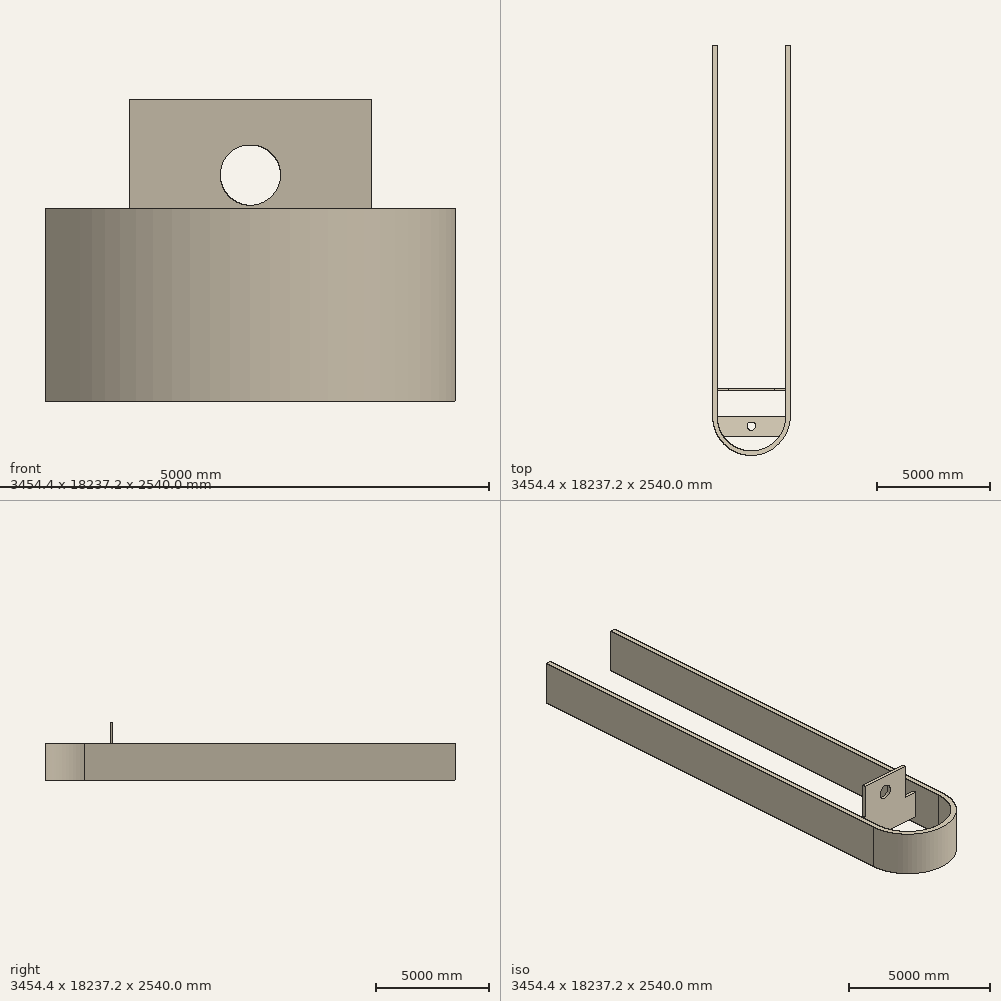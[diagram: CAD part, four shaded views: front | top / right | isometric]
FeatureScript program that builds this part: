
annotation { "Feature Type Name" : "Feature", "Feature Type Description" : "" }
export const myFeature = defineFeature(function(context is Context, id is Id, definition is map)
    precondition{}
    {
        {
            var Q0;
            Q0=qCreatedBy(makeId("Top.planeOp"),FACE);
            var sketch = newSketch(context, id + "F0", { "sketchPlane" : qUnion([Q0])});
            skLineSegment(sketch, "E0", {"start": v(-1727.2, 0) * mm, "end": v(-1524, 0) * mm});
            skLineSegment(sketch, "E1", {"start": v(-1524, 0) * mm, "end": v(-1524, -1270) * mm});
            skLineSegment(sketch, "E2", {"start": v(-1727.2, 0) * mm, "end": v(-1727.2, -1270) * mm});
            skPoint(sketch, "E3.end.orphan", {"position": v(0, -2403.06) * mm});
            skLineSegment(sketch, "E4", {"start": v(1524, -1270) * mm, "end": v(1524, 0) * mm});
            skLineSegment(sketch, "E5", {"start": v(1524, 0) * mm, "end": v(1727.2, 0) * mm});
            skArc(sketch, "E6", {"start": v(1524, -1270) * mm, "mid": v(0, -2794) * mm, "end": v(-1524, -1270) * mm});
            skArc(sketch, "E7", {"start": v(-1727.2, -1270) * mm, "mid": v(0, -2997.2) * mm, "end": v(1727.2, -1270) * mm});
            skLineSegment(sketch, "E8", {"start": v(1727.2, -1270) * mm, "end": v(1727.2, 0) * mm});
            skSolve(sketch);
        }
        {
            var Q0;
            Q0=makeQuery(id+"F0.imprint","IMPRINT",FACE,{"disambiguationData":[TD([[makeQuery(id+"F0.imprint","IMPRINT",EDGE,{"derivedFrom":sQuery(id+"F0.wireOp",EDGE,"E0")}),-1.0]])]});
            extrude(context, id + "F1", {"entities" : qUnion([Q0]), "depth" : 1625.6 * mm});
        }
        {
            var Q0;
            Q0=qCreatedBy(makeId("Front.planeOp"),FACE);
            var sketch = newSketch(context, id + "F2", { "sketchPlane" : qUnion([Q0])});
            skLineSegment(sketch, "E9", {"start": v(-1524, 1270) * mm, "end": v(-1016, 1270) * mm});
            skLineSegment(sketch, "E10", {"start": v(-1016, 1270) * mm, "end": v(-1016, 2540) * mm});
            skLineSegment(sketch, "E11", {"start": v(-1016, 2540) * mm, "end": v(0, 2540) * mm});
            skLineSegment(sketch, "E12", {"start": v(1524, 1270) * mm, "end": v(1016, 1270) * mm});
            skLineSegment(sketch, "E13", {"start": v(1016, 1270) * mm, "end": v(1016, 2540) * mm});
            skLineSegment(sketch, "E14", {"start": v(1016, 2540) * mm, "end": v(0, 2540) * mm});
            skLineSegment(sketch, "E15", {"start": v(-1524, 1270) * mm, "end": v(-1524, 254) * mm});
            skLineSegment(sketch, "E16", {"start": v(1524, 1270) * mm, "end": v(1524, 254) * mm});
            skLineSegment(sketch, "E17", {"start": v(-1524, 254) * mm, "end": v(1524, 254) * mm});
            skSolve(sketch);
        }
        {
            var Q0;
            Q0=makeQuery(id+"F2.imprint","IMPRINT",FACE,{"disambiguationData":[TD([[makeQuery(id+"F2.imprint","IMPRINT",EDGE,{"derivedFrom":sQuery(id+"F2.wireOp",EDGE,"ZSPI5Kq5-j5FG-L9A3-QIDn-ohDjtnUvU4sG")}),-1.0]])]});
            var Q1;
            Q1=makeQuery(id+"F2.imprint","IMPRINT",FACE,{"disambiguationData":[TD([[makeQuery(id+"F2.imprint","IMPRINT",EDGE,{"derivedFrom":sQuery(id+"F2.wireOp",EDGE,"E9")}),-1.0]])]});
            extrude(context, id + "F3", {"entities" : qUnion([Q0, Q1]), "operationType" : NewBodyOperationType.ADD, "depth" : 127 * mm});
        }
        {
            var Q0;
            Q0=makeQuery(id+"F3.boolean.opBoolean","MERGE",FACE,{"derivedFrom":[makeQuery(id+"F1.opExtrude","SWEPT_FACE",FACE,{"disambiguationData":[OSD([sQuery(id+"F0.wireOp",EDGE,"E0")])]}),makeQuery(id+"F1.opExtrude","SWEPT_FACE",FACE,{"disambiguationData":[OSD([sQuery(id+"F0.wireOp",EDGE,"E5")])]}),makeQuery(id+"F3.opExtrude","CAP_FACE",FACE,{"disambiguationData":[OSD([sQuery(id+"F2.wireOp",EDGE,"E9"),sQuery(id+"F2.wireOp",EDGE,"E10"),sQuery(id+"F2.wireOp",EDGE,"E11"),sQuery(id+"F2.wireOp",EDGE,"E12"),sQuery(id+"F2.wireOp",EDGE,"E13"),sQuery(id+"F2.wireOp",EDGE,"E14"),sQuery(id+"F2.wireOp",EDGE,"E15"),sQuery(id+"F2.wireOp",EDGE,"E16"),sQuery(id+"F2.wireOp",EDGE,"E17")])],"isStart":true})]});
            var sketch = newSketch(context, id + "F4", { "sketchPlane" : qUnion([Q0])});
            skPoint(sketch, "E18", {"position": v(0, 1905) * mm});
            skSolve(sketch);
        }
        {
            var Q0;
            Q0=sQuery(id+"F4.wireOp",VERTEX,"E18");
            var Q1;
            Q1=makeQuery(id+"F1.opExtrude","SWEPT_BODY",BODY,{"disambiguationData":[OSD([sQuery(id+"F0.wireOp",EDGE,"E0"),sQuery(id+"F0.wireOp",EDGE,"E1"),sQuery(id+"F0.wireOp",EDGE,"E2"),sQuery(id+"F0.wireOp",EDGE,"9GpaX0HQ-ANni-udGZ-ch0X-FV7p1uEIL64O"),sQuery(id+"F0.wireOp",EDGE,"6B0ilIzi-gSCg-tgtf-X7SF-Btb2jImptZIT"),sQuery(id+"F0.wireOp",EDGE,"E4"),sQuery(id+"F0.wireOp",EDGE,"BRMD6dyG-T5lG-EnZK-6NoF-wr3sixz7AlLv"),sQuery(id+"F0.wireOp",EDGE,"E5")])]});
            hole(context, id + "F5", {"style" : HoleStyle.SIMPLE, "endStyle" : HoleEndStyle.BLIND, "holeDiameter" : 508 * mm, "holeDepth" : 127 * mm, "isTappedThrough" : true, "tappedDepth" : 12.7 * mm, "tapClearance" : 3, "locations" : qUnion([Q0]), "scope" : qUnion([Q1])});
        }
        {
            var Q0;
            Q0=makeQuery(id+"F3.boolean.opBoolean","MERGE",FACE,{"derivedFrom":[makeQuery(id+"F1.opExtrude","SWEPT_FACE",FACE,{"disambiguationData":[OSD([sQuery(id+"F0.wireOp",EDGE,"E0")])]}),makeQuery(id+"F1.opExtrude","SWEPT_FACE",FACE,{"disambiguationData":[OSD([sQuery(id+"F0.wireOp",EDGE,"E5")])]}),makeQuery(id+"F3.opExtrude","CAP_FACE",FACE,{"disambiguationData":[OSD([sQuery(id+"F2.wireOp",EDGE,"E9"),sQuery(id+"F2.wireOp",EDGE,"E10"),sQuery(id+"F2.wireOp",EDGE,"E11"),sQuery(id+"F2.wireOp",EDGE,"E12"),sQuery(id+"F2.wireOp",EDGE,"E13"),sQuery(id+"F2.wireOp",EDGE,"E14"),sQuery(id+"F2.wireOp",EDGE,"E15"),sQuery(id+"F2.wireOp",EDGE,"E16"),sQuery(id+"F2.wireOp",EDGE,"E17")])],"isStart":true})]});
            var sketch = newSketch(context, id + "F6", { "sketchPlane" : qUnion([Q0])});
            skLineSegment(sketch, "E19.bottom", {"start": v(-1524, 1625.6) * mm, "end": v(-1524, 1625.6) * mm});
            skLineSegment(sketch, "E19.top", {"start": v(-1524, 0) * mm, "end": v(-1524, 0) * mm});
            skLineSegment(sketch, "E19.left", {"start": v(-1524, 1625.6) * mm, "end": v(-1524, 0) * mm});
            skLineSegment(sketch, "E19.right", {"start": v(-1524, 1625.6) * mm, "end": v(-1524, 0) * mm});
            skLineSegment(sketch, "E20.bottom", {"start": v(1524, 1625.6) * mm, "end": v(1727.2, 1625.6) * mm});
            skLineSegment(sketch, "E20.top", {"start": v(1524, 0) * mm, "end": v(1727.2, 0) * mm});
            skLineSegment(sketch, "E20.left", {"start": v(1524, 1625.6) * mm, "end": v(1524, 0) * mm});
            skLineSegment(sketch, "E20.right", {"start": v(1727.2, 1625.6) * mm, "end": v(1727.2, 0) * mm});
            skSolve(sketch);
        }
        {
            var Q0;
            {var subQ0=sQuery(id+"F0.wireOp",EDGE,"E5");var subQ2=makeQuery(id+"F1.opExtrude","CAP_EDGE",EDGE,{"disambiguationData":[OSD([subQ0])],"isStart":true});Q0=makeQuery(id+"F6.imprint","IMPRINT",FACE,{"disambiguationData":[TD([[makeQuery(id+"F6.imprint","IMPRINT",EDGE,{"derivedFrom":subQ2}),-1.0]])]});}
            var Q1;
            {var subQ1=sQuery(id+"F6.wireOp",EDGE,"E20.bottom");Q1=makeQuery(id+"F6.imprint","IMPRINT",FACE,{"disambiguationData":[TD([[makeQuery(id+"F6.imprint","IMPRINT",EDGE,{"derivedFrom":subQ1}),1.0]])]});}
            extrude(context, id + "F7", {"entities" : qUnion([Q0, Q1]), "operationType" : NewBodyOperationType.ADD, "depth" : 15240 * mm});
        }
        {
            var Q0;
            {var subQ0=sQuery(id+"F0.wireOp",EDGE,"E5");Q0=makeQuery(id+"F7.boolean.opBoolean","MERGE",FACE,{"derivedFrom":[makeQuery(id+"F1.opExtrude","CAP_FACE",FACE,{"disambiguationData":[OSD([sQuery(id+"F0.wireOp",EDGE,"E0"),sQuery(id+"F0.wireOp",EDGE,"E1"),sQuery(id+"F0.wireOp",EDGE,"E2"),sQuery(id+"F0.wireOp",EDGE,"E4"),subQ0,sQuery(id+"F0.wireOp",EDGE,"E6"),sQuery(id+"F0.wireOp",EDGE,"E7"),sQuery(id+"F0.wireOp",EDGE,"E8")])],"isStart":true}),makeQuery(id+"F7.opExtrude","SWEPT_FACE",FACE,{"disambiguationData":[OSD([sQuery(id+"F6.wireOp",EDGE,"E20.top")])]}),makeQuery(id+"F7.opExtrude","SWEPT_FACE",FACE,{"disambiguationData":[OSD([subQ0]),TDD([makeQuery(id+"F6.imprint","IMPRINT",EDGE,{"derivedFrom":makeQuery(id+"F1.opExtrude","CAP_EDGE",EDGE,{"disambiguationData":[OSD([subQ0])],"isStart":true})})])]})]});}
            var sketch = newSketch(context, id + "F8", { "sketchPlane" : qUnion([Q0])});
            skLineSegment(sketch, "E21", {"start": v(-1524, 1270) * mm, "end": v(1524, 1270) * mm});
            skLineSegment(sketch, "E22", {"start": v(-1243.94, 2150.45) * mm, "end": v(1243.94, 2150.45) * mm});
            skArc(sketch, "E23", {"start": v(-1243.94, 2150.45) * mm, "mid": v(-1452.3, 1731.96) * mm, "end": v(-1524, 1270) * mm});
            skArc(sketch, "E24", {"start": v(1524, 1270) * mm, "mid": v(1452.3, 1731.96) * mm, "end": v(1243.94, 2150.45) * mm});
            skSolve(sketch);
        }
        {
            var Q0;
            Q0 = qSketchRegion(id + "F8", true);
            extrude(context, id + "F9", {"entities" : qUnion([Q0]), "operationType" : NewBodyOperationType.ADD, "oppositeDirection" : true, "depth" : 127 * mm});
        }
        {
            var Q0;
            Q0=makeQuery(id+"F9.opExtrude","CAP_FACE",FACE,{"disambiguationData":[OSD([sQuery(id+"F8.wireOp",EDGE,"E21"),sQuery(id+"F8.wireOp",EDGE,"E22"),sQuery(id+"F8.wireOp",EDGE,"E23"),sQuery(id+"F8.wireOp",EDGE,"E24")])],"isStart":false});
            var sketch = newSketch(context, id + "F10", { "sketchPlane" : qUnion([Q0])});
            skPoint(sketch, "E25", {"position": v(0, -1701.8) * mm});
            skSolve(sketch);
        }
        {
            var Q0;
            Q0=sQuery(id+"F10.wireOp",VERTEX,"E25");
            var Q1;
            Q1=makeQuery(id+"F1.opExtrude","SWEPT_BODY",BODY,{"disambiguationData":[OSD([sQuery(id+"F0.wireOp",EDGE,"E0"),sQuery(id+"F0.wireOp",EDGE,"E1"),sQuery(id+"F0.wireOp",EDGE,"E2"),sQuery(id+"F0.wireOp",EDGE,"E4"),sQuery(id+"F0.wireOp",EDGE,"E5"),sQuery(id+"F0.wireOp",EDGE,"E6"),sQuery(id+"F0.wireOp",EDGE,"E7"),sQuery(id+"F0.wireOp",EDGE,"E8")])]});
            hole(context, id + "F11", {"style" : HoleStyle.SIMPLE, "endStyle" : HoleEndStyle.BLIND, "holeDiameter" : 381 * mm, "holeDepth" : 127 * mm, "isTappedThrough" : true, "tappedDepth" : 12.7 * mm, "tapClearance" : 3, "locations" : qUnion([Q0]), "scope" : qUnion([Q1])});
        }
    });
